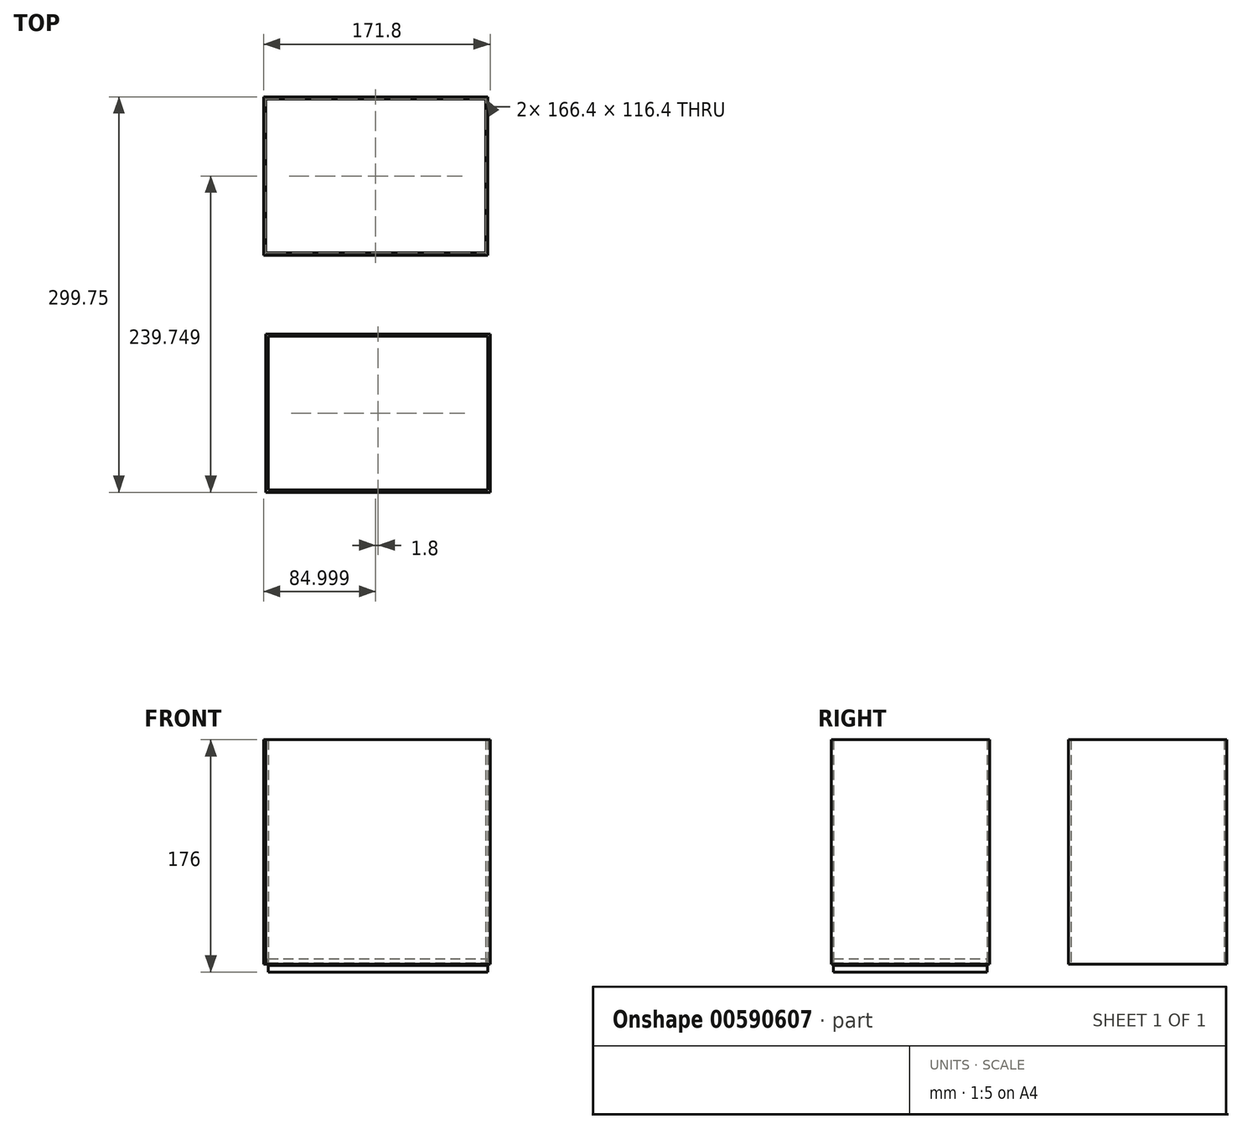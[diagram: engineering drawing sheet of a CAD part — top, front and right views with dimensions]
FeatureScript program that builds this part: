
annotation { "Feature Type Name" : "Feature", "Feature Type Description" : "" }
export const myFeature = defineFeature(function(context is Context, id is Id, definition is map)
    precondition{}
    {
        {
            var Q0;
            Q0=qCreatedBy(makeId("Top.planeOp"),FACE);
            var sketch = newSketch(context, id + "F0", { "sketchPlane" : qUnion([Q0])});
            skLineSegment(sketch, "E0.bottom", {"start": v(-78.22, 181.55) * mm, "end": v(91.78, 181.55) * mm});
            skLineSegment(sketch, "E0.top", {"start": v(-78.22, 61.55) * mm, "end": v(91.78, 61.55) * mm});
            skLineSegment(sketch, "E0.left", {"start": v(-78.22, 181.55) * mm, "end": v(-78.22, 61.55) * mm});
            skLineSegment(sketch, "E0.right", {"start": v(91.78, 181.55) * mm, "end": v(91.78, 61.55) * mm});
            skLineSegment(sketch, "E1.bottom", {"start": v(-76.42, 179.75) * mm, "end": v(89.98, 179.75) * mm});
            skLineSegment(sketch, "E1.top", {"start": v(-76.42, 63.35) * mm, "end": v(89.98, 63.35) * mm});
            skLineSegment(sketch, "E1.left", {"start": v(-76.42, 179.75) * mm, "end": v(-76.42, 63.35) * mm});
            skLineSegment(sketch, "E1.right", {"start": v(89.98, 179.75) * mm, "end": v(89.98, 63.35) * mm});
            skLineSegment(sketch, "E2.bottom", {"start": v(-76.42, -118.2) * mm, "end": v(93.58, -118.2) * mm});
            skLineSegment(sketch, "E2.top", {"start": v(-76.42, 1.8) * mm, "end": v(93.58, 1.8) * mm});
            skLineSegment(sketch, "E2.left", {"start": v(-76.42, -118.2) * mm, "end": v(-76.42, 1.8) * mm});
            skLineSegment(sketch, "E2.right", {"start": v(93.58, -118.2) * mm, "end": v(93.58, 1.8) * mm});
            skLineSegment(sketch, "E3.bottom", {"start": v(-74.62, -116.4) * mm, "end": v(91.78, -116.4) * mm});
            skLineSegment(sketch, "E3.top", {"start": v(-74.62, 0) * mm, "end": v(91.78, 0) * mm});
            skLineSegment(sketch, "E3.left", {"start": v(-74.62, -116.4) * mm, "end": v(-74.62, 0) * mm});
            skLineSegment(sketch, "E3.right", {"start": v(91.78, -116.4) * mm, "end": v(91.78, 0) * mm});
            skSolve(sketch);
        }
        {
            var Q0;
            Q0=makeQuery(id+"F0.imprint","IMPRINT",FACE,{"disambiguationData":[TD([[makeQuery(id+"F0.imprint","IMPRINT",EDGE,{"derivedFrom":sQuery(id+"F0.wireOp",EDGE,"E1.bottom")}),-1.0]])]});
            extrude(context, id + "F1", {"entities" : qUnion([Q0]), "depth" : 170 * mm, "offsetDistance" : 25 * mm});
        }
        {
            var Q0;
            Q0=makeQuery(id+"F0.imprint","IMPRINT",FACE,{"disambiguationData":[TD([[makeQuery(id+"F0.imprint","IMPRINT",EDGE,{"derivedFrom":sQuery(id+"F0.wireOp",EDGE,"E0.bottom")}),-1.0]])]});
            extrude(context, id + "F2", {"entities" : qUnion([Q0]), "depth" : 170 * mm, "offsetDistance" : 25 * mm});
        }
        {
            var Q0;
            Q0=makeQuery(id+"F1.opExtrude","SWEPT_BODY",BODY,{"disambiguationData":[OSD([sQuery(id+"F0.wireOp",EDGE,"E1.bottom"),sQuery(id+"F0.wireOp",EDGE,"E1.top"),sQuery(id+"F0.wireOp",EDGE,"E1.left"),sQuery(id+"F0.wireOp",EDGE,"E1.right")])]});
            var Q1;
            Q1=makeQuery(id+"F2.opExtrude","SWEPT_BODY",BODY,{"disambiguationData":[OSD([sQuery(id+"F0.wireOp",EDGE,"E0.bottom"),sQuery(id+"F0.wireOp",EDGE,"E0.top"),sQuery(id+"F0.wireOp",EDGE,"E0.left"),sQuery(id+"F0.wireOp",EDGE,"E0.right"),sQuery(id+"F0.wireOp",EDGE,"E1.bottom"),sQuery(id+"F0.wireOp",EDGE,"E1.top"),sQuery(id+"F0.wireOp",EDGE,"E1.left"),sQuery(id+"F0.wireOp",EDGE,"E1.right")])]});
            booleanBodies(context, id + "F3", {"operationType" : BooleanOperationType.SUBTRACTION, "tools" : qUnion([Q0]), "targets" : qUnion([Q1])});
        }
        {
            var Q0;
            Q0=makeQuery(id+"F0.imprint","IMPRINT",FACE,{"disambiguationData":[TD([[makeQuery(id+"F0.imprint","IMPRINT",EDGE,{"derivedFrom":sQuery(id+"F0.wireOp",EDGE,"E3.bottom")}),1.0]])]});
            extrude(context, id + "F4", {"entities" : qUnion([Q0]), "endBound" : BoundingType.SYMMETRIC, "depth" : 2 * mm, "offsetDistance" : 25 * mm});
        }
        {
            var Q0;
            Q0=makeQuery(id+"F4.opExtrude","CAP_FACE",FACE,{"disambiguationData":[OSD([sQuery(id+"F0.wireOp",EDGE,"E3.bottom"),sQuery(id+"F0.wireOp",EDGE,"E3.top"),sQuery(id+"F0.wireOp",EDGE,"E3.left"),sQuery(id+"F0.wireOp",EDGE,"E3.right")])],"isStart":true});
            extrude(context, id + "F5", {"entities" : qUnion([Q0]), "endBound" : BoundingType.SYMMETRIC, "depth" : 10 * mm, "offsetDistance" : 25 * mm});
        }
        {
            var Q0;
            Q0=makeQuery(id+"F0.imprint","IMPRINT",FACE,{"disambiguationData":[TD([[makeQuery(id+"F0.imprint","IMPRINT",EDGE,{"derivedFrom":sQuery(id+"F0.wireOp",EDGE,"E2.bottom")}),1.0]])]});
            extrude(context, id + "F6", {"entities" : qUnion([Q0]), "depth" : 170 * mm, "offsetDistance" : 25 * mm});
        }
    });
